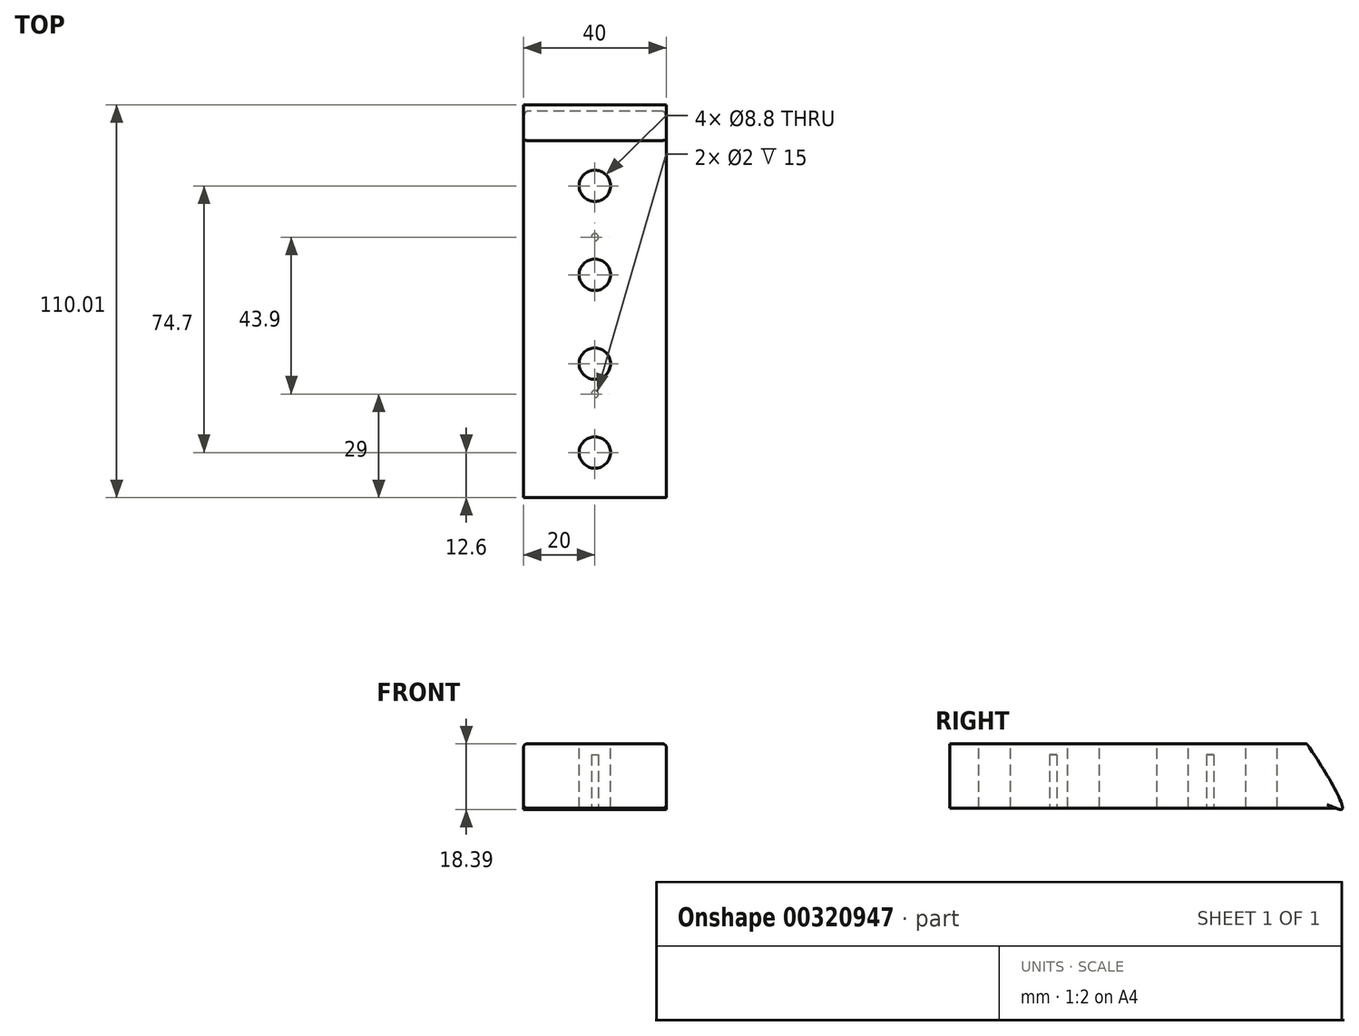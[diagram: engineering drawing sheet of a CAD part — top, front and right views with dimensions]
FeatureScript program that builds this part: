
annotation { "Feature Type Name" : "Feature", "Feature Type Description" : "" }
export const myFeature = defineFeature(function(context is Context, id is Id, definition is map)
    precondition{}
    {
        {
            var Q0;
            Q0=qCreatedBy(makeId("Right.planeOp"),FACE);
            var sketch = newSketch(context, id + "F0", { "sketchPlane" : qUnion([Q0])});
            skLineSegment(sketch, "E0.top", {"start": v(0, -18) * mm, "end": v(110, -18) * mm});
            skLineSegment(sketch, "E0.left", {"start": v(0, 0) * mm, "end": v(0, -18) * mm});
            skLineSegment(sketch, "E0.right", {"start": v(110, -18) * mm, "end": v(110, -18) * mm});
            skFitSpline(sketch, "E1", {"points": [v(100, 0) * mm, v(110, -18) * mm, v(92.42, -15.91) * mm], "startDerivative": vector(12.43, -15.9) * mm, "endDerivative": vector(-60.73, -18.58) * mm});
            skLineSegment(sketch, "E2", {"start": v(0, 0) * mm, "end": v(100, 0) * mm});
            skSolve(sketch);
        }
        {
            var Q0;
            Q0 = qSketchRegion(id + "F0", true);
            extrude(context, id + "F1", {"entities" : qUnion([Q0]), "depth" : 40 * mm});
        }
        {
            var Q0;
            Q0=makeQuery(id+"F1.opExtrude","SWEPT_FACE",FACE,{"disambiguationData":[OSD([sQuery(id+"F0.wireOp",EDGE,"E2")])]});
            var sketch = newSketch(context, id + "F2", { "sketchPlane" : qUnion([Q0])});
            skCircle(sketch, "E3", {"center": v(20, 87.3) * mm, "radius": 4.4 * mm});
            skCircle(sketch, "E4", {"center": v(20, 62.4) * mm, "radius": 4.4 * mm});
            skCircle(sketch, "E5", {"center": v(20, 37.5) * mm, "radius": 4.4 * mm});
            skCircle(sketch, "E6", {"center": v(20, 12.6) * mm, "radius": 4.4 * mm});
            skSolve(sketch);
        }
        {
            var Q0;
            Q0 = qSketchRegion(id + "F2", true);
            extrude(context, id + "F3", {"entities" : qUnion([Q0]), "operationType" : NewBodyOperationType.REMOVE, "endBound" : BoundingType.UP_TO_NEXT, "oppositeDirection" : true, "depth" : 25 * mm});
        }
        {
            var Q0;
            Q0=makeQuery(id+"F1.opExtrude","CAP_EDGE",EDGE,{"disambiguationData":[OSD([sQuery(id+"F0.wireOp",EDGE,"E2")])],"isStart":true});
            var Q1;
            Q1=makeQuery(id+"F1.opExtrude","CAP_EDGE",EDGE,{"disambiguationData":[OSD([sQuery(id+"F0.wireOp",EDGE,"E0.top")])],"isStart":true});
            var Q2;
            Q2=makeQuery(id+"F1.opExtrude","CAP_EDGE",EDGE,{"disambiguationData":[OSD([sQuery(id+"F0.wireOp",EDGE,"E2")])],"isStart":false});
            var Q3;
            Q3=makeQuery(id+"F1.opExtrude","CAP_EDGE",EDGE,{"disambiguationData":[OSD([sQuery(id+"F0.wireOp",EDGE,"E0.top")])],"isStart":false});
            fillet(context, id + "F4", {"entities" : qUnion([Q0, Q1, Q2, Q3]), "radius" : 1 * mm, "tangentPropagation" : true, "allowEdgeOverflow" : false});
        }
        {
            var Q0;
            Q0=makeQuery(id+"F1.opExtrude","SWEPT_FACE",FACE,{"disambiguationData":[OSD([sQuery(id+"F0.wireOp",EDGE,"E0.top")])]});
            var sketch = newSketch(context, id + "F5", { "sketchPlane" : qUnion([Q0])});
            skCircle(sketch, "E7", {"center": v(20, -72.9) * mm, "radius": 1 * mm});
            skCircle(sketch, "E8", {"center": v(20, -29) * mm, "radius": 1 * mm});
            skSolve(sketch);
        }
        {
            var Q0;
            Q0 = qSketchRegion(id + "F5", true);
            extrude(context, id + "F6", {"entities" : qUnion([Q0]), "operationType" : NewBodyOperationType.REMOVE, "oppositeDirection" : true, "depth" : 15 * mm});
        }
    });
